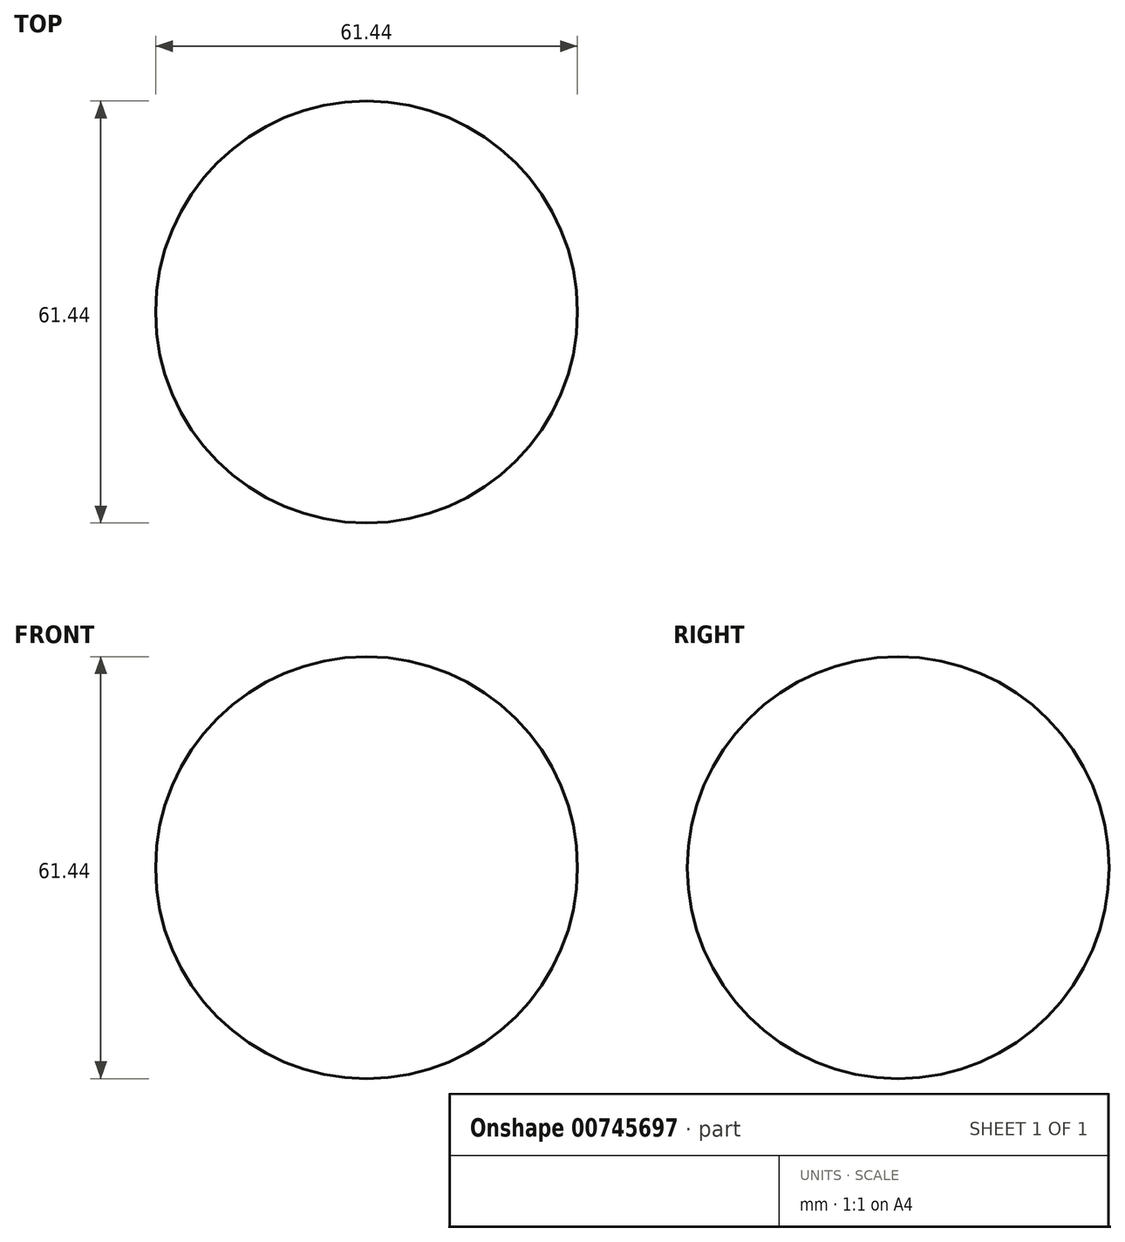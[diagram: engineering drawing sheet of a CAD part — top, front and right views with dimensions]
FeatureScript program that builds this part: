
annotation { "Feature Type Name" : "Feature", "Feature Type Description" : "" }
export const myFeature = defineFeature(function(context is Context, id is Id, definition is map)
    precondition{}
    {
        {
            var Q0;
            Q0=qCreatedBy(makeId("Front.planeOp"),FACE);
            var sketch = newSketch(context, id + "F0", { "sketchPlane" : qUnion([Q0])});
            skArc(sketch, "E0", {"start": v(0, 30.72) * mm, "mid": v(-30.72, 0) * mm, "end": v(0, -30.72) * mm});
            skLineSegment(sketch, "E1", {"start": v(0, -30.72) * mm, "end": v(0, 30.72) * mm});
            skSolve(sketch);
        }
        {
            var Q0;
            Q0=qCreatedBy(makeId("Front.planeOp"),FACE);
            var sketch = newSketch(context, id + "F1", { "sketchPlane" : qUnion([Q0])});
            skLineSegment(sketch, "E2", {"start": v(0, -52.85) * mm, "end": v(0, 60.35) * mm});
            skSolve(sketch);
        }
        {
            var Q0;
            Q0 = qSketchRegion(id + "F0", true);
            var Q1;
            Q1=sQuery(id+"F1.wireOp",EDGE,"E2");
            revolve(context, id + "F2", {"surfaceOperationType" : NewSurfaceOperationType.NEW, "entities" : qUnion([Q0]), "axis" : qUnion([Q1]), "revolveType" : RevolveType.FULL});
        }
    });
